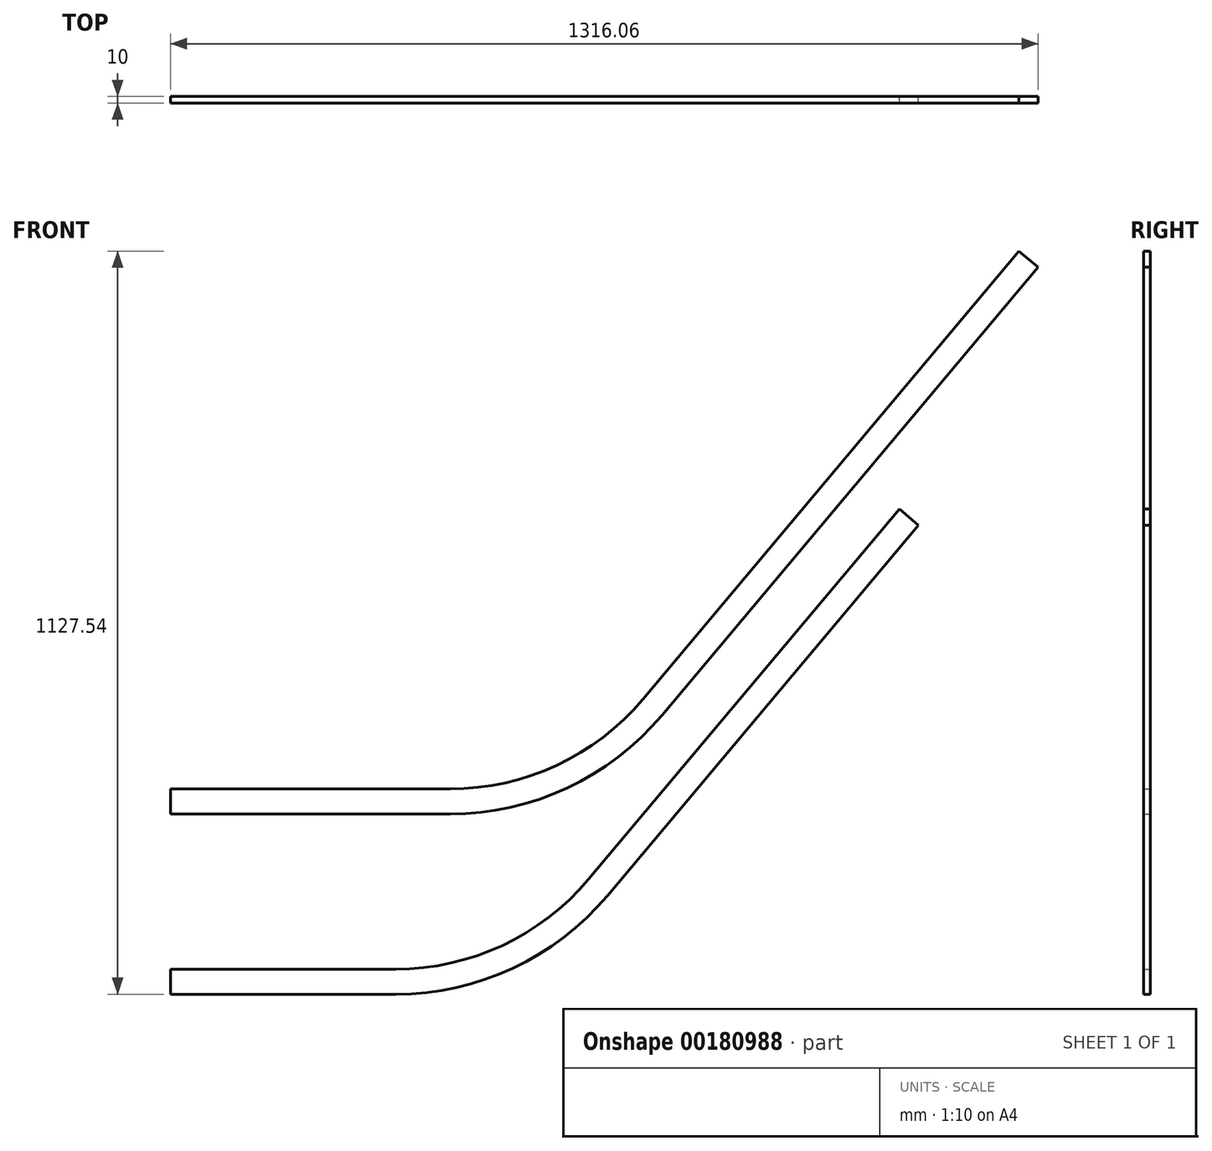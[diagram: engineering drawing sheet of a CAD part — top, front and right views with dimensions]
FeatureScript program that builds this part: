
annotation { "Feature Type Name" : "Feature", "Feature Type Description" : "" }
export const myFeature = defineFeature(function(context is Context, id is Id, definition is map)
    precondition{}
    {
        {
            var Q0;
            Q0=qCreatedBy(makeId("Front.planeOp"),FACE);
            var sketch = newSketch(context, id + "F0", { "sketchPlane" : qUnion([Q0])});
            skLineSegment(sketch, "E0", {"start": v(0, 0) * mm, "end": v(600, 0) * mm});
            skLineSegment(sketch, "E1", {"start": v(600, 0) * mm, "end": v(2600, 2383.5) * mm});
            skLineSegment(sketch, "E2", {"start": v(2600, 2383.5) * mm, "end": v(3200, 2383.5) * mm});
            skLineSegment(sketch, "E3", {"start": v(600, 0) * mm, "end": v(910.54, 0) * mm, "construction": true});
            skLineSegment(sketch, "E4", {"start": v(730.97, 516.38) * mm, "end": v(792.77, 590.03) * mm});
            skPoint(sketch, "E5", {"position": v(761.87, 553.2) * mm});
            skPoint(sketch, "E6", {"position": v(661.87, 317.2) * mm});
            skCircle(sketch, "E7", {"center": v(661.87, 317.2) * mm, "radius": 18.5 * mm, "construction": true});
            skLineSegment(sketch, "E8", {"start": v(454.53, 41.33) * mm, "end": v(1105.55, 817.18) * mm});
            skLineSegment(sketch, "E9", {"start": v(586.5, 139.48) * mm, "end": v(1189.81, 858.49) * mm});
            skLineSegment(sketch, "E10", {"start": v(745.53, 504.17) * mm, "end": v(1316.06, 1184.1) * mm});
            skLineSegment(sketch, "E11", {"start": v(689.93, 497.02) * mm, "end": v(1816.6, 1839.73) * mm});
            skLineSegment(sketch, "E12", {"start": v(374.56, 373.5) * mm, "end": v(424.56, 373.5) * mm});
            skArc(sketch, "E13", {"start": v(424.56, 373.5) * mm, "mid": v(593.6, 410.98) * mm, "end": v(730.97, 516.38) * mm});
            skLineSegment(sketch, "E14", {"start": v(424.56, 373.5) * mm, "end": v(424.56, 773.5) * mm, "construction": true});
            skLineSegment(sketch, "E15", {"start": v(424.56, 773.5) * mm, "end": v(730.97, 516.38) * mm, "construction": true});
            skLineSegment(sketch, "E16", {"start": v(0, 0) * mm, "end": v(0, 732.21) * mm, "construction": true});
            skLineSegment(sketch, "E17", {"start": v(374.56, 373.5) * mm, "end": v(0, 373.5) * mm});
            skLineSegment(sketch, "E18", {"start": v(648.46, 242.88) * mm, "end": v(1099.7, 780.64) * mm});
            skArc(sketch, "E19", {"start": v(342.04, 100) * mm, "mid": v(511.1, 137.48) * mm, "end": v(648.46, 242.88) * mm});
            skLineSegment(sketch, "E20", {"start": v(342.04, 100) * mm, "end": v(342.04, 500) * mm, "construction": true});
            skLineSegment(sketch, "E21", {"start": v(342.04, 500) * mm, "end": v(648.46, 242.88) * mm, "construction": true});
            skLineSegment(sketch, "E22", {"start": v(342.04, 100) * mm, "end": v(292.04, 100) * mm});
            skLineSegment(sketch, "E23", {"start": v(292.04, 100) * mm, "end": v(0, 100) * mm});
            skLineSegment(sketch, "E24", {"start": v(1316.06, 1184.1) * mm, "end": v(1286.96, 1208.54) * mm});
            skArc(sketch, "E25.0", {"start": v(424.56, 392.5) * mm, "mid": v(585.57, 428.2) * mm, "end": v(716.42, 528.6) * mm});
            skArc(sketch, "E26.0", {"start": v(424.56, 354.5) * mm, "mid": v(601.63, 393.76) * mm, "end": v(745.53, 504.17) * mm});
            skLineSegment(sketch, "E27", {"start": v(424.56, 392.5) * mm, "end": v(0, 392.5) * mm});
            skLineSegment(sketch, "E28", {"start": v(0, 392.5) * mm, "end": v(0, 354.5) * mm});
            skLineSegment(sketch, "E29", {"start": v(0, 354.5) * mm, "end": v(424.56, 354.5) * mm});
            skArc(sketch, "E30.0", {"start": v(342.04, 81) * mm, "mid": v(519.12, 120.26) * mm, "end": v(663.02, 230.67) * mm});
            skArc(sketch, "E31.0", {"start": v(342.04, 119) * mm, "mid": v(503.06, 154.7) * mm, "end": v(633.9, 255.1) * mm});
            skLineSegment(sketch, "E32", {"start": v(342.04, 119) * mm, "end": v(0, 119) * mm});
            skLineSegment(sketch, "E33", {"start": v(342.04, 81) * mm, "end": v(0, 81) * mm});
            skLineSegment(sketch, "E34", {"start": v(0, 81) * mm, "end": v(0, 119) * mm});
            skLineSegment(sketch, "E35", {"start": v(1105.55, 817.18) * mm, "end": v(1134.66, 792.76) * mm});
            skSolve(sketch);
        }
        {
            var Q0;
            Q0=makeQuery(id+"F0.imprint","IMPRINT",FACE,{"disambiguationData":[TD([[makeQuery(id+"F0.imprint","IMPRINT",EDGE,{"derivedFrom":sQuery(id+"F0.wireOp",EDGE,"E10")}),1.0]])]});
            var Q1;
            {var subQ3=sQuery(id+"F0.wireOp",EDGE,"E22");Q1=makeQuery(id+"F0.imprint","IMPRINT",FACE,{"disambiguationData":[TD([[makeQuery(id+"F0.imprint","IMPRINT",EDGE,{"derivedFrom":subQ3}),1.0]])]});}
            var Q2;
            {var subQ5=sQuery(id+"F0.wireOp",EDGE,"E22");Q2=makeQuery(id+"F0.imprint","IMPRINT",FACE,{"disambiguationData":[TD([[makeQuery(id+"F0.imprint","IMPRINT",EDGE,{"derivedFrom":subQ5}),-1.0]])]});}
            var Q3;
            {var subQ3=sQuery(id+"F0.wireOp",EDGE,"E35");Q3=makeQuery(id+"F0.imprint","IMPRINT",FACE,{"disambiguationData":[TD([[makeQuery(id+"F0.imprint","IMPRINT",EDGE,{"derivedFrom":subQ3}),-1.0]])]});}
            extrude(context, id + "F1", {"entities" : qUnion([Q0, Q1, Q2, Q3]), "depth" : 10 * mm});
        }
    });
